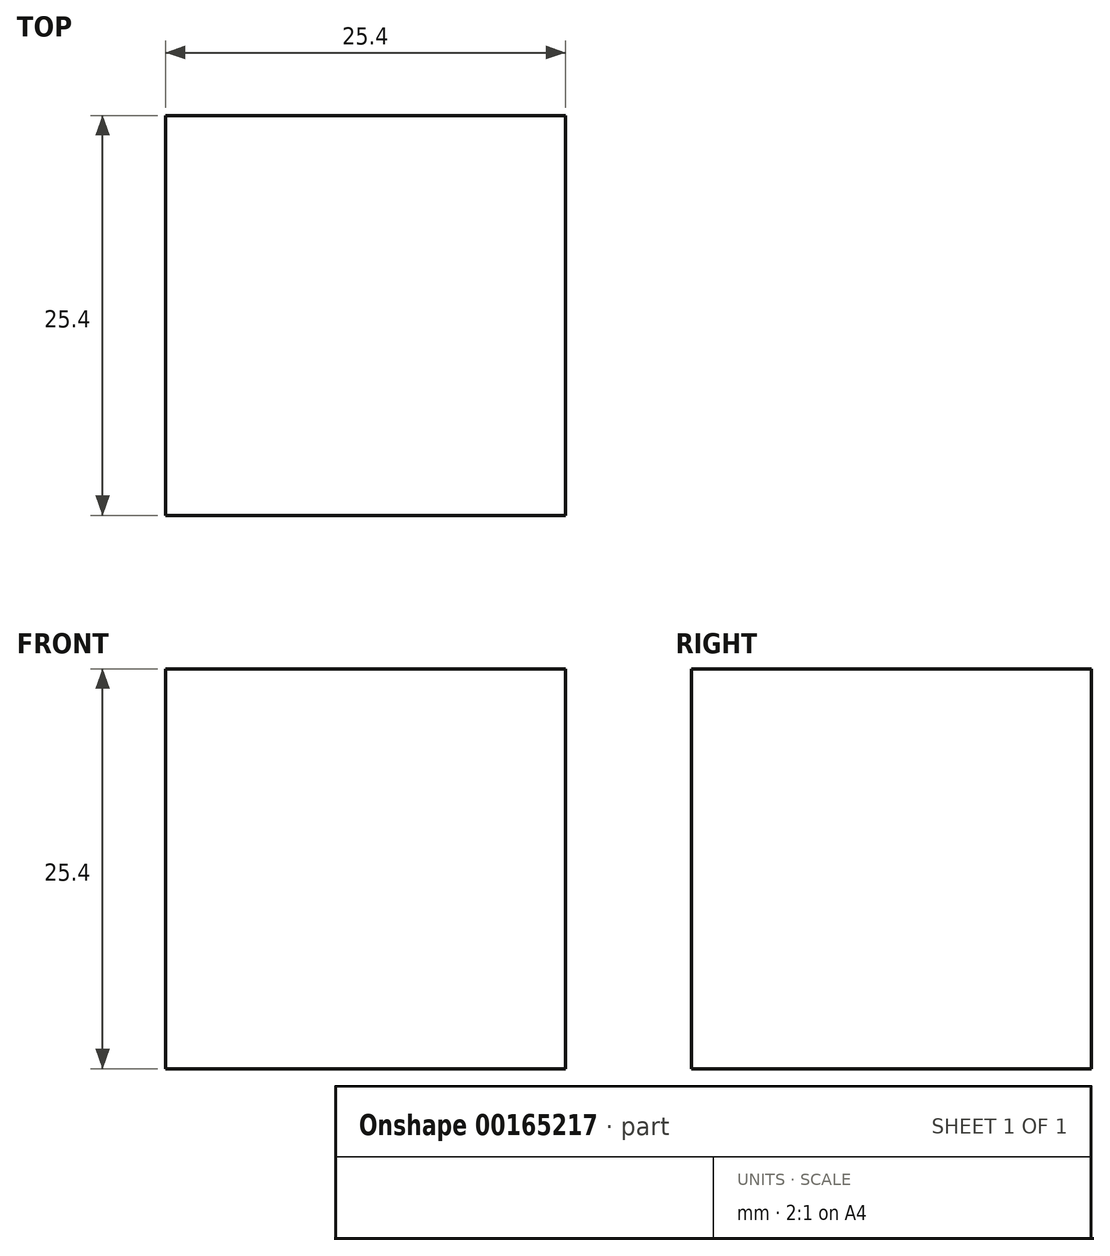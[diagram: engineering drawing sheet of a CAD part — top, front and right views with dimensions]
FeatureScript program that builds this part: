
annotation { "Feature Type Name" : "Feature", "Feature Type Description" : "" }
export const myFeature = defineFeature(function(context is Context, id is Id, definition is map)
    precondition{}
    {
        {
            var Q0;
            Q0=qCreatedBy(makeId("Top.planeOp"),FACE);
            var sketch = newSketch(context, id + "F0", { "sketchPlane" : qUnion([Q0])});
            skLineSegment(sketch, "E0.bottom", {"start": v(0, 0) * mm, "end": v(25.4, 0) * mm});
            skLineSegment(sketch, "E0.top", {"start": v(0, 25.4) * mm, "end": v(25.4, 25.4) * mm});
            skLineSegment(sketch, "E0.left", {"start": v(0, 0) * mm, "end": v(0, 25.4) * mm});
            skLineSegment(sketch, "E0.right", {"start": v(25.4, 0) * mm, "end": v(25.4, 25.4) * mm});
            skSolve(sketch);
        }
        {
            var Q0;
            Q0=qSketchRegion(id+"F0",true);
            extrude(context, id + "F1", {"entities" : qUnion([Q0]), "depth" : 25.4 * mm});
        }
    });
